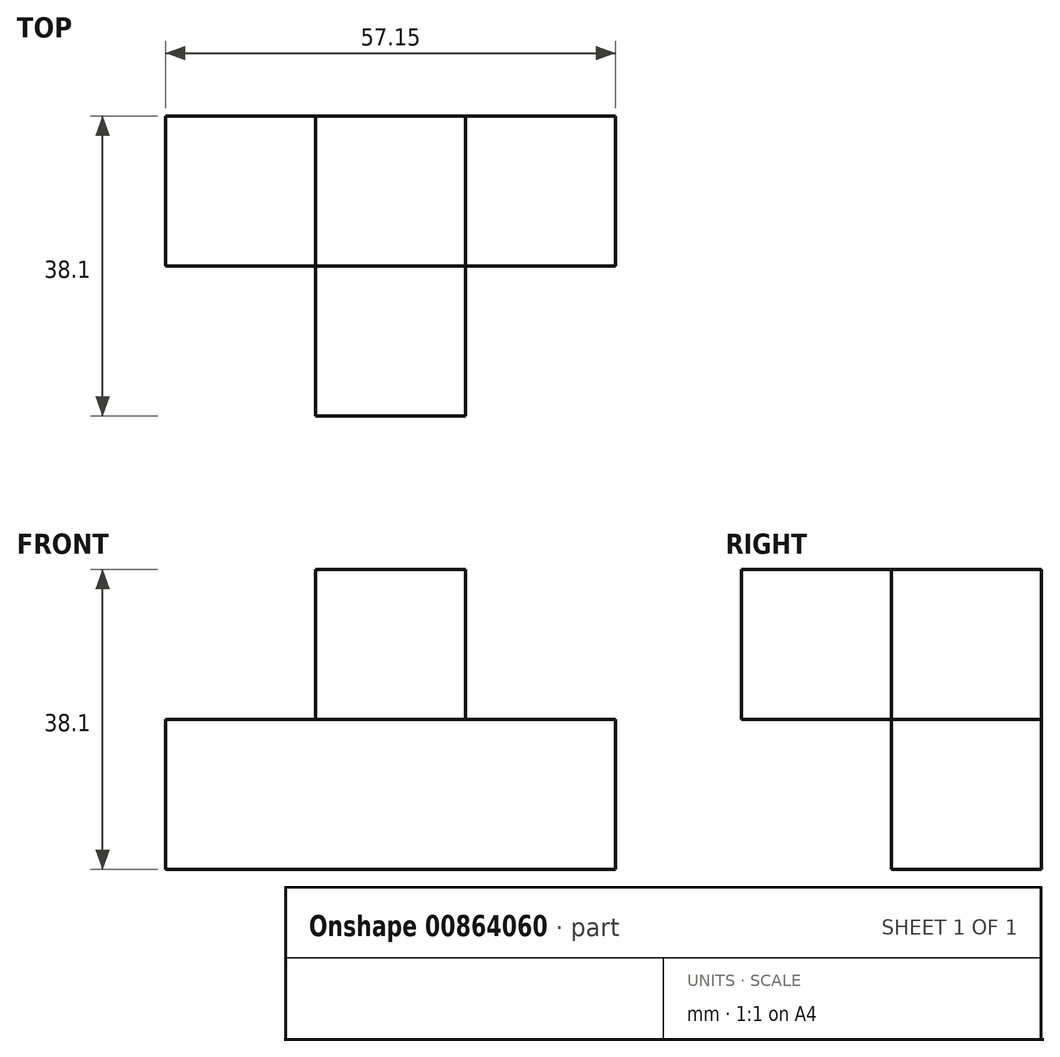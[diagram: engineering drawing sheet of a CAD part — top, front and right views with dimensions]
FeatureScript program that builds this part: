
annotation { "Feature Type Name" : "Feature", "Feature Type Description" : "" }
export const myFeature = defineFeature(function(context is Context, id is Id, definition is map)
    precondition{}
    {
        {
            var Q0;
            Q0=qCreatedBy(makeId("Front.planeOp"),FACE);
            var sketch = newSketch(context, id + "F0", { "sketchPlane" : qUnion([Q0])});
            skLineSegment(sketch, "E0", {"start": v(0, 0) * mm, "end": v(57.15, 0) * mm});
            skLineSegment(sketch, "E1", {"start": v(57.15, 0) * mm, "end": v(57.15, 19.05) * mm});
            skLineSegment(sketch, "E2", {"start": v(57.15, 19.05) * mm, "end": v(38.1, 19.05) * mm});
            skLineSegment(sketch, "E3", {"start": v(38.1, 19.05) * mm, "end": v(38.1, 38.1) * mm});
            skLineSegment(sketch, "E4", {"start": v(38.1, 38.1) * mm, "end": v(19.05, 38.1) * mm});
            skLineSegment(sketch, "E5", {"start": v(19.05, 38.1) * mm, "end": v(19.05, 19.05) * mm});
            skLineSegment(sketch, "E6", {"start": v(19.05, 19.05) * mm, "end": v(0, 19.05) * mm});
            skLineSegment(sketch, "E7", {"start": v(0, 19.05) * mm, "end": v(0, 0) * mm});
            skSolve(sketch);
        }
        {
            var Q0;
            Q0 = qSketchRegion(id + "F0", true);
            extrude(context, id + "F1", {"entities" : qUnion([Q0]), "depth" : 19.05 * mm, "offsetDistance" : 25.4 * mm});
        }
        {
            var Q0;
            Q0=makeQuery(id+"F1.opExtrude","CAP_FACE",FACE,{"disambiguationData":[OSD([sQuery(id+"F0.wireOp",EDGE,"E0"),sQuery(id+"F0.wireOp",EDGE,"E1"),sQuery(id+"F0.wireOp",EDGE,"E2"),sQuery(id+"F0.wireOp",EDGE,"E3"),sQuery(id+"F0.wireOp",EDGE,"E4"),sQuery(id+"F0.wireOp",EDGE,"E5"),sQuery(id+"F0.wireOp",EDGE,"E6"),sQuery(id+"F0.wireOp",EDGE,"E7")])],"isStart":false});
            var sketch = newSketch(context, id + "F2", { "sketchPlane" : qUnion([Q0])});
            skLineSegment(sketch, "E8.0.0", {"start": v(19.05, 19.05) * mm, "end": v(0, 19.05) * mm});
            skLineSegment(sketch, "E8.0.1", {"start": v(0, 19.05) * mm, "end": v(0, 0) * mm});
            skLineSegment(sketch, "E8.0.2", {"start": v(0, 0) * mm, "end": v(57.15, 0) * mm});
            skLineSegment(sketch, "E8.0.3", {"start": v(57.15, 0) * mm, "end": v(57.15, 19.05) * mm});
            skLineSegment(sketch, "E8.0.4", {"start": v(57.15, 19.05) * mm, "end": v(38.1, 19.05) * mm});
            skLineSegment(sketch, "E8.0.5", {"start": v(38.1, 19.05) * mm, "end": v(38.1, 38.1) * mm});
            skLineSegment(sketch, "E8.0.6", {"start": v(38.1, 38.1) * mm, "end": v(19.05, 38.1) * mm});
            skLineSegment(sketch, "E8.0.7", {"start": v(19.05, 38.1) * mm, "end": v(19.05, 19.05) * mm});
            skLineSegment(sketch, "E9", {"start": v(19.05, 19.05) * mm, "end": v(38.1, 19.05) * mm});
            skSolve(sketch);
        }
        {
            var Q0;
            Q0=makeQuery(id+"F2.imprint","IMPRINT",FACE,{"disambiguationData":[TD([[makeQuery(id+"F2.imprint","IMPRINT",EDGE,{"derivedFrom":sQuery(id+"F2.wireOp",EDGE,"E8.0.5")}),1.0]])]});
            extrude(context, id + "F3", {"entities" : qUnion([Q0]), "depth" : 19.05 * mm, "offsetDistance" : 25.4 * mm});
        }
    });
